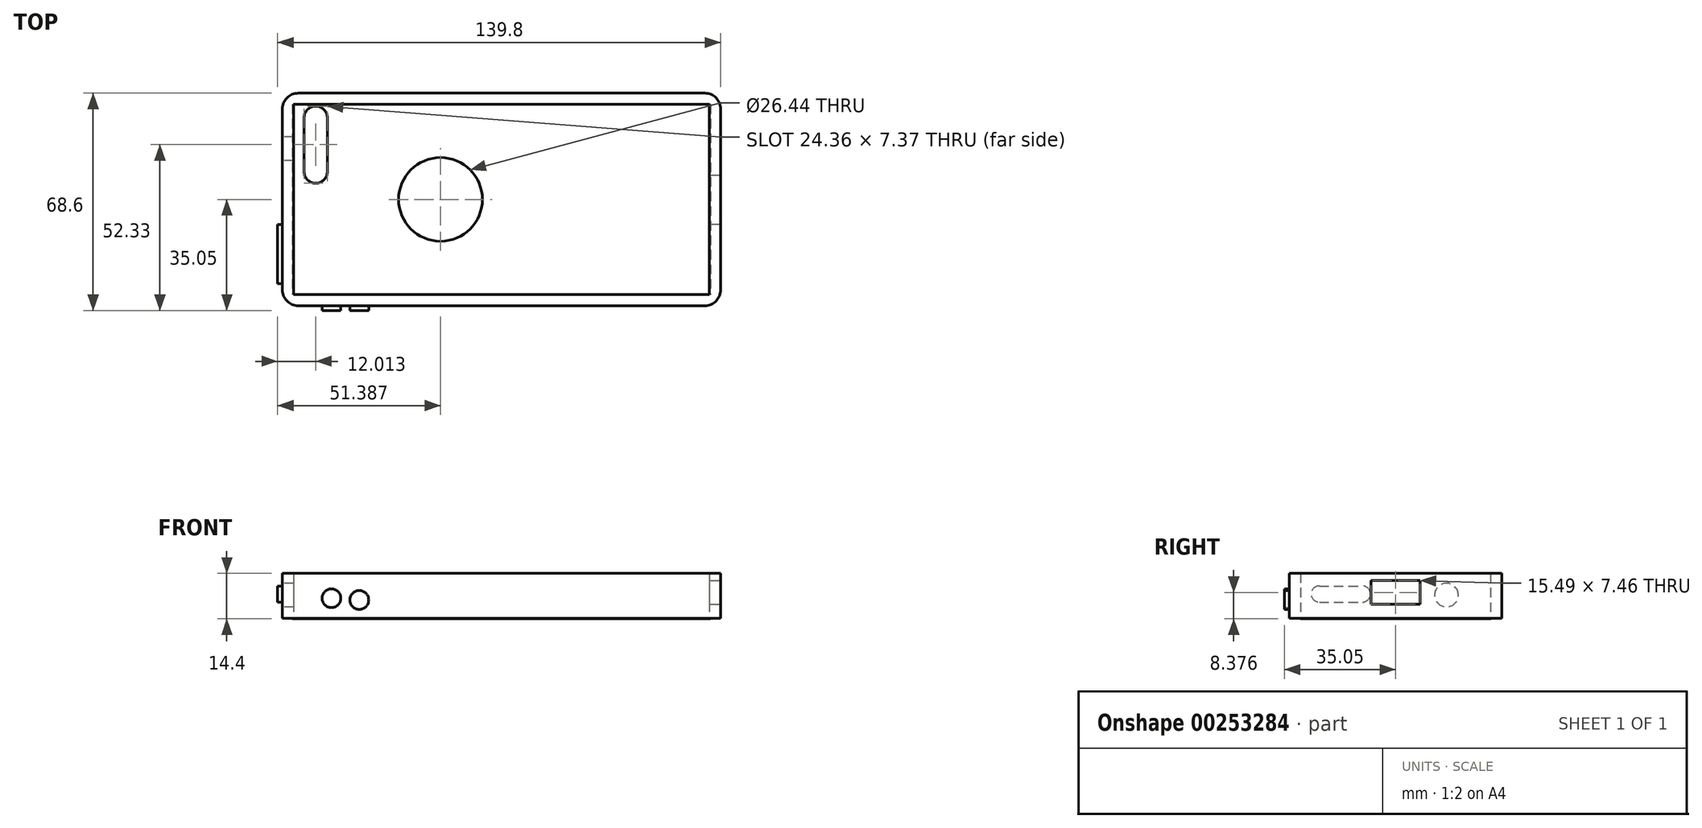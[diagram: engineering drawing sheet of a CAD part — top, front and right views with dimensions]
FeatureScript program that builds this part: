
annotation { "Feature Type Name" : "Feature", "Feature Type Description" : "" }
export const myFeature = defineFeature(function(context is Context, id is Id, definition is map)
    precondition{}
    {
        {
            var Q0;
            Q0=qCreatedBy(makeId("Top.planeOp"),FACE);
            var sketch = newSketch(context, id + "F0", { "sketchPlane" : qUnion([Q0])});
            skLineSegment(sketch, "E0.bottom", {"start": v(69.15, -33.55) * mm, "end": v(-69.15, -33.55) * mm});
            skLineSegment(sketch, "E0.top", {"start": v(69.15, 33.55) * mm, "end": v(-69.15, 33.55) * mm});
            skLineSegment(sketch, "E0.left", {"start": v(69.15, -33.55) * mm, "end": v(69.15, 33.55) * mm});
            skLineSegment(sketch, "E0.right", {"start": v(-69.15, -33.55) * mm, "end": v(-69.15, 33.55) * mm});
            skPoint(sketch, "E0.middle", {"position": v(0, 0) * mm});
            skLineSegment(sketch, "E1.bottom", {"start": v(65.6, -30) * mm, "end": v(-65.6, -30) * mm});
            skLineSegment(sketch, "E1.top", {"start": v(65.6, 30) * mm, "end": v(-65.6, 30) * mm});
            skLineSegment(sketch, "E1.left", {"start": v(65.6, -30) * mm, "end": v(65.6, 30) * mm});
            skLineSegment(sketch, "E1.right", {"start": v(-65.6, -30) * mm, "end": v(-65.6, 30) * mm});
            skSolve(sketch);
        }
        {
            var Q0;
            Q0=qSketchRegion(id+"F0",true);
            extrude(context, id + "F1", {"entities" : qUnion([Q0]), "depth" : 14.2 * mm});
        }
        {
            var Q0;
            Q0=makeQuery(id+"F1.opExtrude","SWEPT_EDGE",EDGE,{"disambiguationData":[OSD([sQuery(id+"F0.wireOp",EDGE,"E0.top"),sQuery(id+"F0.wireOp",EDGE,"E0.left")])]});
            var Q1;
            Q1=makeQuery(id+"F1.opExtrude","SWEPT_EDGE",EDGE,{"disambiguationData":[OSD([sQuery(id+"F0.wireOp",EDGE,"E0.bottom"),sQuery(id+"F0.wireOp",EDGE,"E0.left")])]});
            var Q2;
            Q2=makeQuery(id+"F1.opExtrude","SWEPT_EDGE",EDGE,{"disambiguationData":[OSD([sQuery(id+"F0.wireOp",EDGE,"E0.bottom"),sQuery(id+"F0.wireOp",EDGE,"E0.right")])]});
            var Q3;
            Q3=makeQuery(id+"F1.opExtrude","SWEPT_EDGE",EDGE,{"disambiguationData":[OSD([sQuery(id+"F0.wireOp",EDGE,"E0.top"),sQuery(id+"F0.wireOp",EDGE,"E0.right")])]});
            fillet(context, id + "F2", {"entities" : qUnion([Q0, Q1, Q2, Q3]), "radius" : 5 * mm, "tangentPropagation" : true, "allowEdgeOverflow" : false});
        }
        {
            var Q0;
            Q0=qCreatedBy(makeId("Top.planeOp"),FACE);
            var sketch = newSketch(context, id + "F3", { "sketchPlane" : qUnion([Q0])});
            skLineSegment(sketch, "E2.bottom", {"start": v(66, 30.03) * mm, "end": v(-66, 30.03) * mm});
            skLineSegment(sketch, "E2.top", {"start": v(66, -30.03) * mm, "end": v(-66, -30.03) * mm});
            skLineSegment(sketch, "E2.left", {"start": v(66, 30.03) * mm, "end": v(66, -30.03) * mm});
            skLineSegment(sketch, "E2.right", {"start": v(-66, 30.03) * mm, "end": v(-66, -30.03) * mm});
            skPoint(sketch, "E2.middle", {"position": v(0, 0) * mm});
            skCircle(sketch, "E3", {"center": v(-19.26, 0) * mm, "radius": 13.22 * mm});
            skLineSegment(sketch, "E4.bottom", {"start": v(-54.96, 25.78) * mm, "end": v(-62.32, 25.78) * mm});
            skLineSegment(sketch, "E4.top", {"start": v(-54.96, 8.78) * mm, "end": v(-62.32, 8.78) * mm});
            skLineSegment(sketch, "E4.left", {"start": v(-54.96, 25.78) * mm, "end": v(-54.96, 8.78) * mm});
            skLineSegment(sketch, "E4.right", {"start": v(-62.32, 25.78) * mm, "end": v(-62.32, 8.78) * mm});
            skPoint(sketch, "E4.middle", {"position": v(-58.64, 17.28) * mm});
            skArc(sketch, "E5", {"start": v(-62.32, 8.78) * mm, "mid": v(-58.64, 5.1) * mm, "end": v(-54.96, 8.78) * mm});
            skArc(sketch, "E6", {"start": v(-54.96, 25.78) * mm, "mid": v(-58.64, 29.46) * mm, "end": v(-62.32, 25.78) * mm});
            skSolve(sketch);
        }
        {
            var Q0;
            Q0=qSketchRegion(id+"F3",true);
            extrude(context, id + "F4", {"entities" : qUnion([Q0]), "operationType" : NewBodyOperationType.ADD, "oppositeDirection" : true, "depth" : 0.2 * mm});
        }
        {
            var Q0;
            Q0=makeQuery(id+"F1.opExtrude","SWEPT_FACE",FACE,{"disambiguationData":[OSD([sQuery(id+"F0.wireOp",EDGE,"E0.bottom")])]});
            var sketch = newSketch(context, id + "F5", { "sketchPlane" : qUnion([Q0])});
            skCircle(sketch, "E7", {"center": v(-53.68, 6.33) * mm, "radius": 2.97 * mm});
            skCircle(sketch, "E8", {"center": v(-44.9, 5.77) * mm, "radius": 2.98 * mm});
            skSolve(sketch);
        }
        {
            var Q0;
            Q0=qSketchRegion(id+"F5",true);
            extrude(context, id + "F6", {"entities" : qUnion([Q0]), "operationType" : NewBodyOperationType.ADD, "depth" : 1.5 * mm});
        }
        {
            var Q0;
            Q0=makeQuery(id+"F1.opExtrude","SWEPT_FACE",FACE,{"disambiguationData":[OSD([sQuery(id+"F0.wireOp",EDGE,"E0.right")])]});
            var sketch = newSketch(context, id + "F7", { "sketchPlane" : qUnion([Q0])});
            skLineSegment(sketch, "E9.bottom", {"start": v(24.08, 5.1) * mm, "end": v(10.48, 5.1) * mm});
            skLineSegment(sketch, "E9.top", {"start": v(24.08, 10.2) * mm, "end": v(10.48, 10.2) * mm});
            skLineSegment(sketch, "E9.left", {"start": v(24.08, 5.1) * mm, "end": v(24.08, 10.2) * mm});
            skLineSegment(sketch, "E9.right", {"start": v(10.48, 5.1) * mm, "end": v(10.48, 10.2) * mm});
            skPoint(sketch, "E9.middle", {"position": v(17.28, 7.65) * mm});
            skArc(sketch, "E10", {"start": v(10.48, 10.2) * mm, "mid": v(7.93, 7.65) * mm, "end": v(10.48, 5.1) * mm});
            skArc(sketch, "E11", {"start": v(24.08, 5.1) * mm, "mid": v(26.63, 7.65) * mm, "end": v(24.08, 10.2) * mm});
            skSolve(sketch);
        }
        {
            var Q0;
            Q0=qSketchRegion(id+"F7",true);
            extrude(context, id + "F8", {"entities" : qUnion([Q0]), "operationType" : NewBodyOperationType.ADD, "depth" : 1.5 * mm});
        }
        {
            var Q0;
            Q0=makeQuery(id+"F1.opExtrude","SWEPT_FACE",FACE,{"disambiguationData":[OSD([sQuery(id+"F0.wireOp",EDGE,"E0.right")])]});
            var sketch = newSketch(context, id + "F9", { "sketchPlane" : qUnion([Q0])});
            skCircle(sketch, "E12", {"center": v(-16.07, 7.32) * mm, "radius": 3.74 * mm});
            skSolve(sketch);
        }
        {
            var Q0;
            Q0 = qSketchRegion(id + "F9", true);
            extrude(context, id + "F10", {"entities" : qUnion([Q0]), "operationType" : NewBodyOperationType.REMOVE, "oppositeDirection" : true, "depth" : 24 * mm});
        }
        {
            var Q0;
            Q0=makeQuery(id+"F1.opExtrude","SWEPT_FACE",FACE,{"disambiguationData":[OSD([sQuery(id+"F0.wireOp",EDGE,"E0.left")])]});
            var sketch = newSketch(context, id + "F11", { "sketchPlane" : qUnion([Q0])});
            skLineSegment(sketch, "E13.bottom", {"start": v(7.75, 4.45) * mm, "end": v(-7.75, 4.45) * mm});
            skLineSegment(sketch, "E13.top", {"start": v(7.75, 11.9) * mm, "end": v(-7.75, 11.9) * mm});
            skLineSegment(sketch, "E13.left", {"start": v(7.75, 4.45) * mm, "end": v(7.75, 11.9) * mm});
            skLineSegment(sketch, "E13.right", {"start": v(-7.75, 4.45) * mm, "end": v(-7.75, 11.9) * mm});
            skPoint(sketch, "E13.middle", {"position": v(0, 8.18) * mm});
            skSolve(sketch);
        }
        {
            var Q0;
            Q0 = qSketchRegion(id + "F11", true);
            extrude(context, id + "F12", {"entities" : qUnion([Q0]), "operationType" : NewBodyOperationType.REMOVE, "oppositeDirection" : true, "depth" : 25 * mm});
        }
    });
